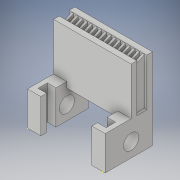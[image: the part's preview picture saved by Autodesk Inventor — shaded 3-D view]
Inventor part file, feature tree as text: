
AUTODESK INVENTOR PART (.ipt)
format: ipt  version: 2018 (Build 220112000, 112)  size: 275,968 bytes
history: native  units: in
note: dims shown in document units (in); Inventor stores cm internally (conversion verified against a paired STEP export)
features: sketch x10, extrude x8, pattern_linear x1, draft x1
ambient origin geometry x8: Origin, YZ Plane, XZ Plane, XY Plane, X Axis, Y Axis, Z Axis, Center Point
bodies: Solid1 (feature_tree)
feature tree (20):
  sketch  "Sketch1"  dims[d0=0.2756in d1=0.9843in]
  extrude  "Extrusion1"  Depth=0.9843in
  sketch  "Sketch3"  dims[d4=0.7087in d5=0.0in d6=0.1181in]
  sketch  "Sketch4"  dims[d7=0.1772in d8=0.1772in]
  extrude  "Extrusion2"  Depth=0.2756in
  extrude  "Extrusion3"  Depth=0.1181in
  extrude  "Extrusion4"  Depth=0.1772in
  sketch  "Sketch6"  dims[d11=0.1181in d12=0.2067in]
  extrude  "Extrusion5"  Depth=0.1969in
  extrude  "Extrusion6"  Depth=0.2067in
  pattern_linear  "Rectangular Pattern1"  Spacing1=0.315in  [1 undecoded]
  sketch  "Sketch9"  dims[d16=0.9843in d17=0.0in]
  extrude  "Extrusion7"  Depth=0.0984in
  draft  "FaceDraft1"
  extrude  "Extrusion8"  Depth=0.0433in
  sketch  "Sketch2"  dims[d2=1.063in d3=0.2756in]
  sketch  "Sketch5"  dims[d9=0.1969in d10=0.1969in]
  sketch  "Sketch7"  dims[d13=0.1181in]
  sketch  "Sketch8"  dims[d14=0.7087in d15=0.0in]
  sketch  "Sketch10"  dims[d18=0.9843in d19=0.0in d20=0.315in d21=0.0787in d22=0.0433in d23=0.1732in d24=0.9843in d25=0.0in d26=0.9843in d27=0.0in d28=6.2992in d30=0.0984in d31=10.0394in d32=0.0in d33=0.1718in d34=0.0in d35=0.0in]
note: 1 required parameter value undecoded (feature->parameter linkage not recoverable at this tier; creation-order binding heuristic only, values carry confidence <= 0.55)
